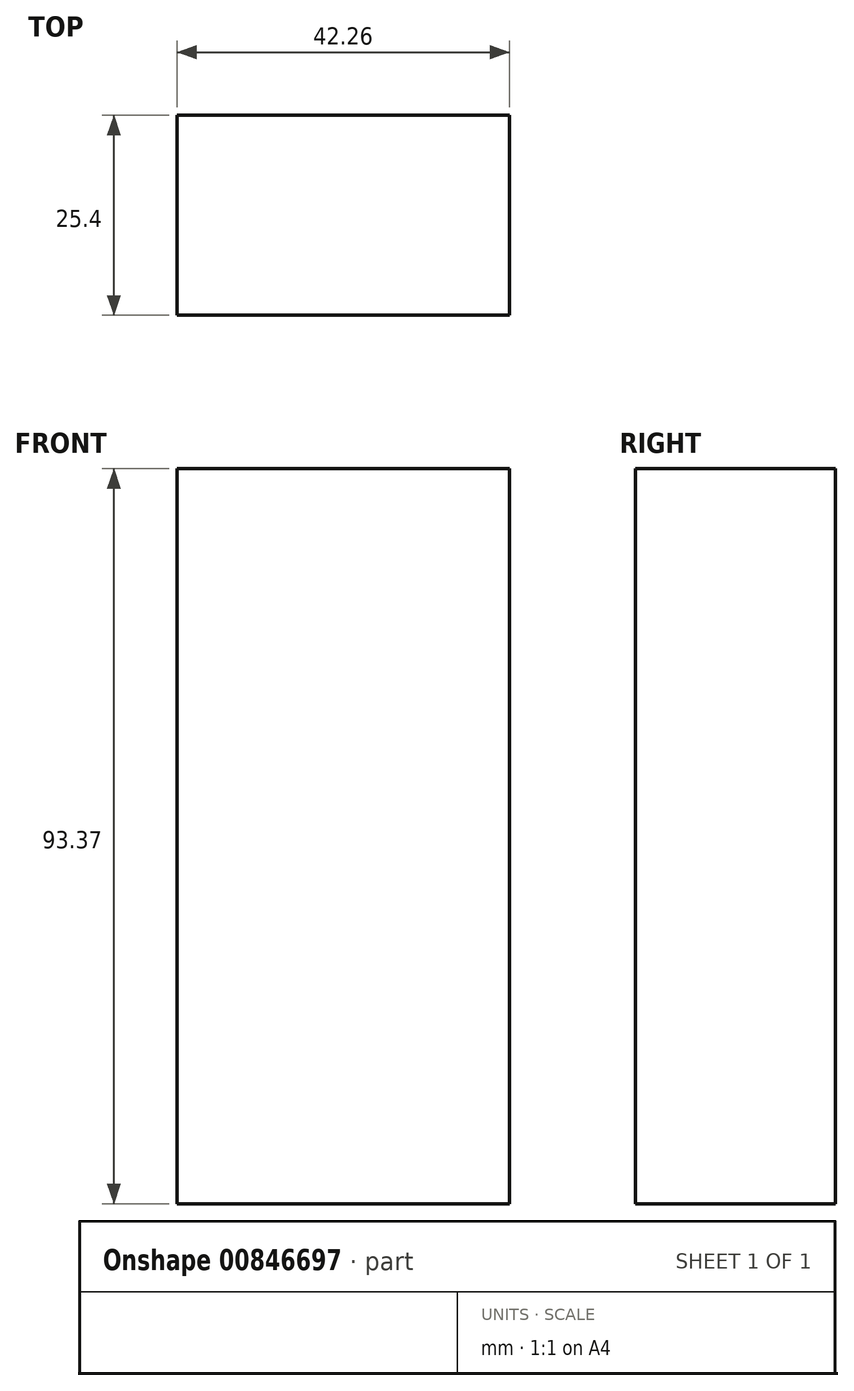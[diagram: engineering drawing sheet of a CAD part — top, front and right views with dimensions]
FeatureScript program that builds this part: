
annotation { "Feature Type Name" : "Feature", "Feature Type Description" : "" }
export const myFeature = defineFeature(function(context is Context, id is Id, definition is map)
    precondition{}
    {
        {
            var Q0;
            Q0=qCreatedBy(makeId("Front.planeOp"),FACE);
            var sketch = newSketch(context, id + "F0", { "sketchPlane" : qUnion([Q0])});
            skLineSegment(sketch, "E0.bottom", {"start": v(-60.75, 34.09) * mm, "end": v(8.4, 34.09) * mm});
            skLineSegment(sketch, "E0.top", {"start": v(-60.75, -59.28) * mm, "end": v(8.4, -59.28) * mm});
            skLineSegment(sketch, "E0.left", {"start": v(-60.75, 34.09) * mm, "end": v(-60.75, -59.28) * mm});
            skLineSegment(sketch, "E0.right", {"start": v(8.4, 34.09) * mm, "end": v(8.4, -59.28) * mm});
            skSolve(sketch);
        }
        {
            var Q0;
            Q0=makeQuery(id+"F0.imprint","IMPRINT",FACE,{"disambiguationData":[TD([[makeQuery(id+"F0.imprint","IMPRINT",EDGE,{"derivedFrom":sQuery(id+"F0.wireOp",EDGE,"E0.bottom")}),-1.0]])]});
            var sketch = newSketch(context, id + "F1", { "sketchPlane" : qUnion([Q0])});
            skLineSegment(sketch, "E1.bottom", {"start": v(-54.5, 43.1) * mm, "end": v(-12.25, 43.1) * mm});
            skLineSegment(sketch, "E1.top", {"start": v(-54.5, -88.78) * mm, "end": v(-12.25, -88.78) * mm});
            skLineSegment(sketch, "E1.left", {"start": v(-54.5, 43.1) * mm, "end": v(-54.5, -88.78) * mm});
            skLineSegment(sketch, "E1.right", {"start": v(-12.25, 43.1) * mm, "end": v(-12.25, -88.78) * mm});
            skSolve(sketch);
        }
        {
            var Q0;
            {var subQ0=sQuery(id+"F1.wireOp",EDGE,"E1.left");var subQ1=makeQuery(id+"F0.imprint","IMPRINT",EDGE,{"derivedFrom":sQuery(id+"F0.wireOp",EDGE,"E0.bottom")});var subQ2=makeQuery(id+"F1.imprint","INTERSECT",VERTEX,{"derivedFrom":[subQ1,subQ0]});Q0=makeQuery(id+"F1.imprint","IMPRINT",FACE,{"disambiguationData":[TD([[makeQuery(id+"F1.imprint","IMPRINT",EDGE,{"disambiguationData":[TD([[subQ2,-1.0]])],"derivedFrom":subQ0}),1.0]])]});}
            extrude(context, id + "F2", {"entities" : qUnion([Q0]), "depth" : 25.4 * mm, "offsetDistance" : 25.4 * mm});
        }
    });
